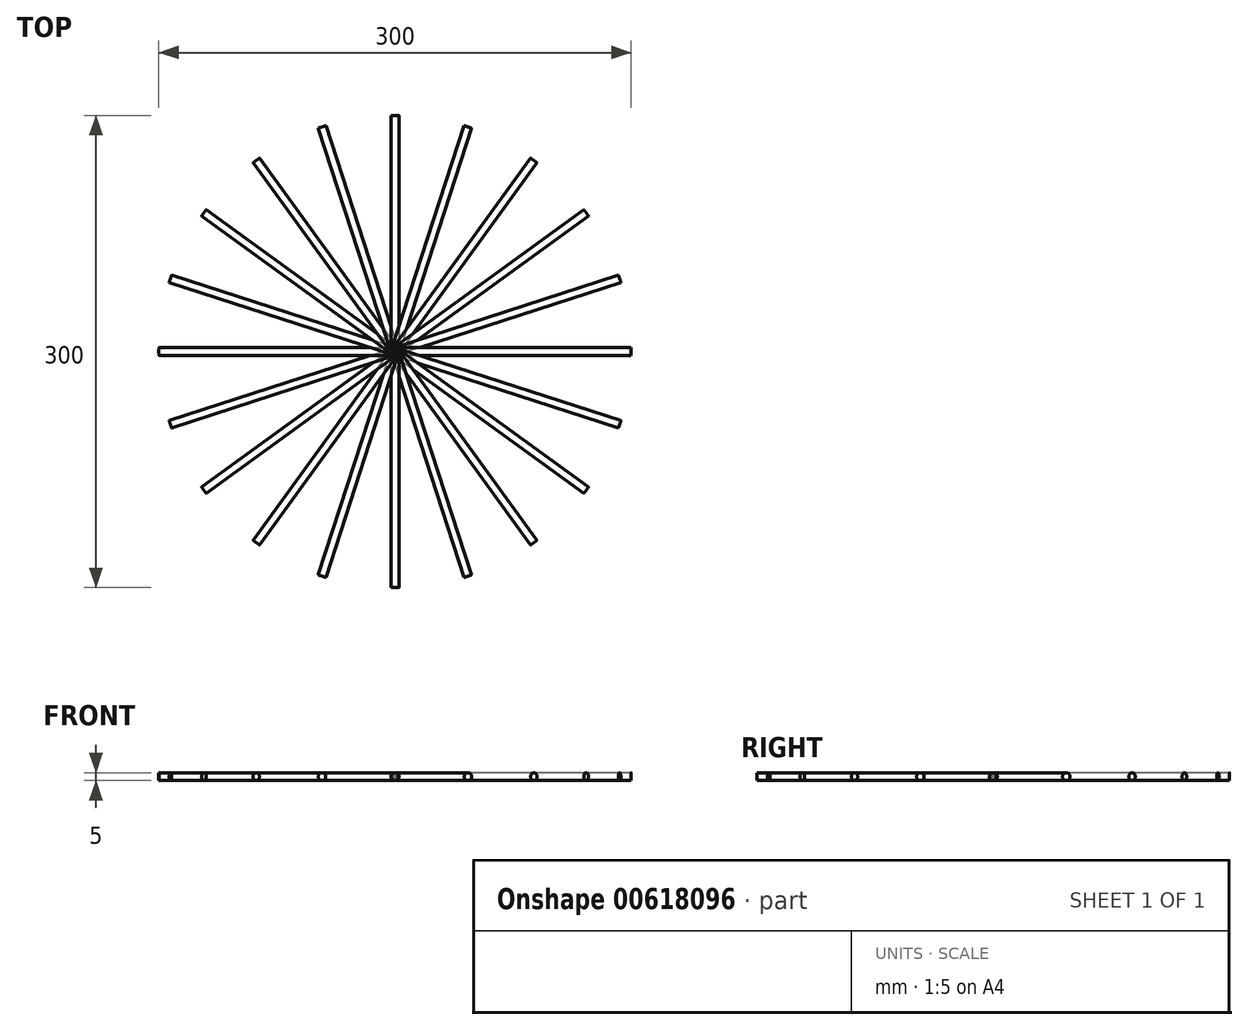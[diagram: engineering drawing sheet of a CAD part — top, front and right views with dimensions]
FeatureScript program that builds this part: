
annotation { "Feature Type Name" : "Feature", "Feature Type Description" : "" }
export const myFeature = defineFeature(function(context is Context, id is Id, definition is map)
    precondition{}
    {
        {
            var Q0;
            Q0=qCreatedBy(makeId("Front.planeOp"),FACE);
            var sketch = newSketch(context, id + "F0", { "sketchPlane" : qUnion([Q0])});
            skLineSegment(sketch, "E0.bottom", {"start": v(-160, 17.44) * mm, "end": v(-150, 17.44) * mm});
            skLineSegment(sketch, "E0.top", {"start": v(-160, -17.44) * mm, "end": v(-150, -17.44) * mm});
            skLineSegment(sketch, "E0.left", {"start": v(-160, 17.44) * mm, "end": v(-160, 8.48) * mm});
            skLineSegment(sketch, "E0.right", {"start": v(0, 17.44) * mm, "end": v(0, -17.44) * mm});
            skLineSegment(sketch, "E1.bottom", {"start": v(-151.34, -8.48) * mm, "end": v(-160, -8.48) * mm});
            skLineSegment(sketch, "E1.top", {"start": v(-151.34, 8.48) * mm, "end": v(-160, 8.48) * mm});
            skLineSegment(sketch, "E1.left", {"start": v(-151.34, -8.48) * mm, "end": v(-151.34, 8.48) * mm});
            skPoint(sketch, "E1.middle", {"position": v(-160, 0) * mm});
            skPoint(sketch, "E1.right.end.orphan", {"position": v(-168.66, 8.48) * mm});
            skPoint(sketch, "E2.orphan", {"position": v(-168.66, -8.48) * mm});
            skLineSegment(sketch, "E3.trimOffspring", {"start": v(-160, -8.48) * mm, "end": v(-160, -17.44) * mm});
            skLineSegment(sketch, "E4", {"start": v(0, 0) * mm, "end": v(0.03, 0) * mm, "construction": true});
            skLineSegment(sketch, "E5", {"start": v(-3, -4.9) * mm, "end": v(-5, -4.9) * mm});
            skLineSegment(sketch, "E6", {"start": v(-5, -4.9) * mm, "end": v(-6.79, -2.26) * mm});
            skLineSegment(sketch, "E7", {"start": v(-6.79, -2.26) * mm, "end": v(-10.3, -2.26) * mm});
            skLineSegment(sketch, "E8", {"start": v(-10.3, -2.26) * mm, "end": v(-10.3, -1.5) * mm});
            skLineSegment(sketch, "E9", {"start": v(-10.3, -1.5) * mm, "end": v(-6.79, -1.5) * mm});
            skLineSegment(sketch, "E10", {"start": v(-6.79, -1.5) * mm, "end": v(-6.79, 0) * mm});
            skLineSegment(sketch, "E11", {"start": v(-6.79, 0) * mm, "end": v(-6.79, 1.5) * mm});
            skLineSegment(sketch, "E12", {"start": v(-6.79, 1.5) * mm, "end": v(-10.3, 1.5) * mm});
            skLineSegment(sketch, "E13", {"start": v(-10.3, 1.5) * mm, "end": v(-10.3, 2.26) * mm});
            skLineSegment(sketch, "E14", {"start": v(-10.3, 2.26) * mm, "end": v(-6.79, 2.26) * mm});
            skLineSegment(sketch, "E15", {"start": v(-6.79, 2.26) * mm, "end": v(-5, 4.9) * mm});
            skLineSegment(sketch, "E16", {"start": v(-5, 4.9) * mm, "end": v(-3, 4.9) * mm});
            skLineSegment(sketch, "E17", {"start": v(-3, 4.9) * mm, "end": v(-3, -4.9) * mm});
            skLineSegment(sketch, "E18", {"start": v(-131.09, 0) * mm, "end": v(-160, 0) * mm, "construction": true});
            skLineSegment(sketch, "E19", {"start": v(-158.35, 0) * mm, "end": v(-158.35, -6.9) * mm});
            skLineSegment(sketch, "E20", {"start": v(-158.35, -6.9) * mm, "end": v(-161, -6.9) * mm});
            skLineSegment(sketch, "E21", {"start": v(-161, -6.9) * mm, "end": v(-161, -17.44) * mm});
            skLineSegment(sketch, "E22", {"start": v(-161, -17.44) * mm, "end": v(-178.6, -17.44) * mm});
            skLineSegment(sketch, "E23", {"start": v(-179.6, -16.44) * mm, "end": v(-179.6, 16.44) * mm});
            skLineSegment(sketch, "E24", {"start": v(-178.6, 17.44) * mm, "end": v(-161, 17.44) * mm});
            skLineSegment(sketch, "E25", {"start": v(-161, 17.44) * mm, "end": v(-161, 6.9) * mm});
            skLineSegment(sketch, "E26", {"start": v(-161, 6.9) * mm, "end": v(-158.35, 6.9) * mm});
            skLineSegment(sketch, "E27", {"start": v(-158.35, 6.9) * mm, "end": v(-158.35, 0) * mm});
            skPoint(sketch, "E28.visualSharp", {"position": v(-179.6, 17.44) * mm});
            skArc(sketch, "E28.filletArc", {"start": v(-178.6, 17.44) * mm, "mid": v(-179.31, 17.15) * mm, "end": v(-179.6, 16.44) * mm});
            skPoint(sketch, "E29.visualSharp", {"position": v(-179.6, -17.44) * mm});
            skArc(sketch, "E29.filletArc", {"start": v(-179.6, -16.44) * mm, "mid": v(-179.31, -17.15) * mm, "end": v(-178.6, -17.44) * mm});
            skLineSegment(sketch, "E30", {"start": v(-150, 17.44) * mm, "end": v(-150, -17.44) * mm});
            skLineSegment(sketch, "E31.bottom", {"start": v(-178.6, 5.66) * mm, "end": v(-180.6, 5.66) * mm});
            skLineSegment(sketch, "E31.top", {"start": v(-178.6, 11.3) * mm, "end": v(-180.6, 11.3) * mm});
            skLineSegment(sketch, "E31.left", {"start": v(-178.6, 5.66) * mm, "end": v(-178.6, 11.3) * mm});
            skLineSegment(sketch, "E31.right", {"start": v(-180.6, 5.66) * mm, "end": v(-180.6, 11.3) * mm});
            skPoint(sketch, "E31.middle", {"position": v(-179.6, 8.48) * mm});
            skLineSegment(sketch, "E32.bottom", {"start": v(-178.6, -5.38) * mm, "end": v(-180.6, -5.38) * mm});
            skLineSegment(sketch, "E32.top", {"start": v(-178.6, -11.59) * mm, "end": v(-180.6, -11.59) * mm});
            skLineSegment(sketch, "E32.left", {"start": v(-178.6, -5.38) * mm, "end": v(-178.6, -11.59) * mm});
            skLineSegment(sketch, "E32.right", {"start": v(-180.6, -5.38) * mm, "end": v(-180.6, -11.59) * mm});
            skPoint(sketch, "E32.middle", {"position": v(-179.6, -8.48) * mm});
            skSolve(sketch);
        }
        {
            var Q0;
            Q0=makeQuery(id+"F0.imprint","IMPRINT",FACE,{"disambiguationData":[TD([[makeQuery(id+"F0.imprint","IMPRINT",EDGE,{"derivedFrom":sQuery(id+"F0.wireOp",EDGE,"E0.bottom")}),-1.0]])]});
            var Q1;
            Q1=sQuery(id+"F0.wireOp",EDGE,"E9");
            var Q2;
            Q2=sQuery(id+"F0.wireOp",EDGE,"E14");
            var Q3;
            Q3=sQuery(id+"F0.wireOp",EDGE,"E17");
            var Q4;
            Q4=sQuery(id+"F0.wireOp",EDGE,"E15");
            var Q5;
            Q5=sQuery(id+"F0.wireOp",EDGE,"E12");
            var Q6;
            Q6=sQuery(id+"F0.wireOp",EDGE,"E7");
            var Q7;
            Q7=sQuery(id+"F0.wireOp",EDGE,"E6");
            var Q8;
            Q8=sQuery(id+"F0.wireOp",EDGE,"E13");
            var Q9;
            Q9=sQuery(id+"F0.wireOp",EDGE,"E10");
            var Q10;
            Q10=sQuery(id+"F0.wireOp",EDGE,"E16");
            var Q11;
            Q11=sQuery(id+"F0.wireOp",EDGE,"E8");
            var Q12;
            Q12=sQuery(id+"F0.wireOp",EDGE,"E5");
            var Q13;
            Q13=sQuery(id+"F0.wireOp",EDGE,"E11");
            var Q14;
            Q14=sQuery(id+"F0.wireOp",EDGE,"E30");
            var Q15;
            Q15=sQuery(id+"F0.wireOp",EDGE,"E0.bottom");
            var Q16;
            Q16=sQuery(id+"F0.wireOp",EDGE,"E21");
            var Q17;
            Q17=sQuery(id+"F0.wireOp",EDGE,"E0.top");
            var Q18;
            Q18=sQuery(id+"F0.wireOp",EDGE,"E0.left");
            var Q19;
            Q19=sQuery(id+"F0.wireOp",EDGE,"E25");
            var Q20;
            Q20=sQuery(id+"F0.wireOp",EDGE,"E23");
            var Q21;
            Q21=sQuery(id+"F0.wireOp",EDGE,"E3.trimOffspring");
            var Q22;
            Q22=sQuery(id+"F0.wireOp",EDGE,"E22");
            var Q23;
            Q23=sQuery(id+"F0.wireOp",EDGE,"E1.left");
            var Q24;
            Q24=sQuery(id+"F0.wireOp",EDGE,"E29.filletArc");
            var Q25;
            Q25=sQuery(id+"F0.wireOp",EDGE,"E24");
            var Q26;
            Q26=sQuery(id+"F0.wireOp",EDGE,"E1.top");
            var Q27;
            Q27=sQuery(id+"F0.wireOp",EDGE,"E1.bottom");
            var Q28;
            Q28=sQuery(id+"F0.wireOp",EDGE,"E28.filletArc");
            var Q29;
            Q29=sQuery(id+"F0.wireOp",EDGE,"E27");
            var Q30;
            Q30=sQuery(id+"F0.wireOp",EDGE,"E26");
            var Q31;
            Q31=sQuery(id+"F0.wireOp",EDGE,"E20");
            var Q32;
            Q32=sQuery(id+"F0.wireOp",EDGE,"E19");
            var Q33;
            Q33=sQuery(id+"F0.wireOp",EDGE,"E0.right");
            revolve(context, id + "F1", {"bodyType" : ToolBodyType.SURFACE, "entities" : qUnion([Q0]), "surfaceEntities" : qUnion([Q1, Q2, Q3, Q4, Q5, Q6, Q7, Q8, Q9, Q10, Q11, Q12, Q13, Q14, Q15, Q16, Q17, Q18, Q19, Q20, Q21, Q22, Q23, Q24, Q25, Q26, Q27, Q28, Q29, Q30, Q31, Q32]), "axis" : qUnion([Q33]), "revolveType" : RevolveType.FULL});
        }
        {
            var Q0;
            Q0=qCreatedBy(makeId("Right.planeOp"),FACE);
            var sketch = newSketch(context, id + "F2", { "sketchPlane" : qUnion([Q0])});
            skCircle(sketch, "E33", {"center": v(0, 0) * mm, "radius": 2.5 * mm});
            skSolve(sketch);
        }
        {
            var Q0;
            Q0=makeQuery(id+"F2.imprint","IMPRINT",FACE,{"disambiguationData":[TD([[makeQuery(id+"F2.imprint","IMPRINT",EDGE,{"derivedFrom":sQuery(id+"F2.wireOp",EDGE,"E33")}),1.0]])]});
            var Q1;
            Q1=makeQuery(id+"F1.opRevolve","SWEPT_FACE",FACE,{"disambiguationData":[OSD([sQuery(id+"F0.wireOp",EDGE,"E30")])]});
            extrude(context, id + "F3", {"entities" : qUnion([Q0]), "endBound" : BoundingType.UP_TO_SURFACE, "depth" : 70.87 * mm, "endBoundEntityFace" : qUnion([Q1]), "offsetDistance" : 25.4 * mm});
        }
        {
            var Q0;
            Q0=makeQuery(id+"F3.opExtrude","SWEPT_BODY",BODY,{"disambiguationData":[OSD([sQuery(id+"F2.wireOp",EDGE,"E33")])]});
            var Q1;
            Q1=makeQuery(id+"F1.opRevolve","SWEPT_EDGE",EDGE,{"disambiguationData":[OSD([sQuery(id+"F0.wireOp",VERTEX,"E5.start")])]});
            circularPattern(context, id + "F4", {"entities" : qUnion([Q0]), "axis" : qUnion([Q1]), "angle" : 360 * degree, "instanceCount" : 20, "oppositeDirection" : true, "equalSpace" : true});
        }
    });
